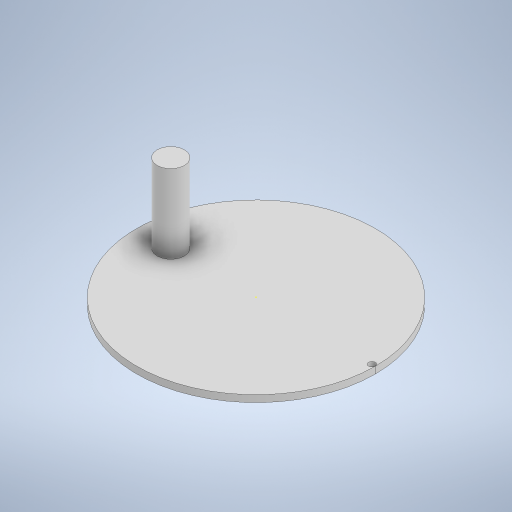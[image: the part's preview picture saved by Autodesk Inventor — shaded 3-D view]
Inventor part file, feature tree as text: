
AUTODESK INVENTOR PART (.ipt)
format: ipt  version: 2024.3 (Build 283343000, 343)  size: 233,472 bytes
history: native  units: mm
features: sketch x3, extrude x3
ambient origin geometry x8: Origin, YZ Plane, XZ Plane, XY Plane, X Axis, Y Axis, Z Axis, Center Point
bodies: Solid1 (feature_tree)
feature tree (6):
  sketch  "Sketch1"  dims[d0=70.0mm d1=8.0mm]
  extrude  "Extrusion1"  Depth=8.0mm
  extrude  "Extrusion2"  Depth=2.0mm TaperAngle=0.0deg
  sketch  "Sketch2"  dims[d2=25.0mm d3=2.0mm d4=0.0mm]
  extrude  "Extrusion3"  Depth=2.0mm
  sketch  "Sketch3"  dims[d5=25.0mm d6=0.0mm d7=2.0mm d8=34.0mm d9=0.0mm d10=0.0mm]
